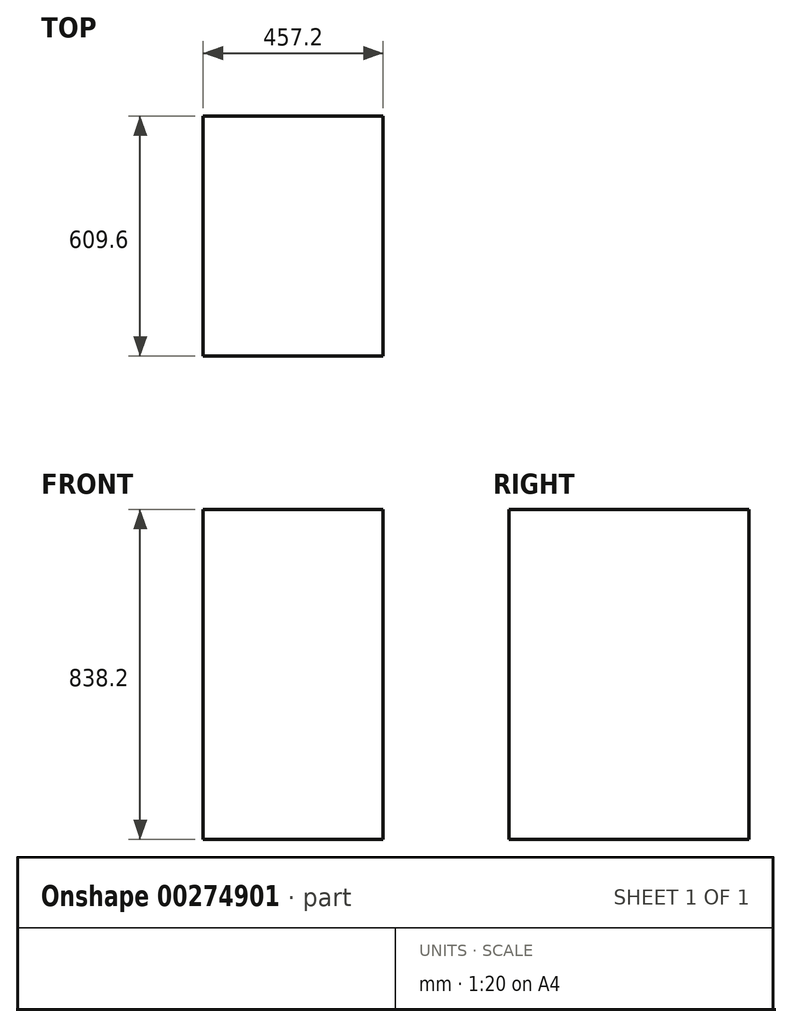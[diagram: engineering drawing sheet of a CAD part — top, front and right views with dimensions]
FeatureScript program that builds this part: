
annotation { "Feature Type Name" : "Feature", "Feature Type Description" : "" }
export const myFeature = defineFeature(function(context is Context, id is Id, definition is map)
    precondition{}
    {
        {
            var Q0;
            Q0=qCreatedBy(makeId("Top.planeOp"),FACE);
            var sketch = newSketch(context, id + "F0", { "sketchPlane" : qUnion([Q0])});
            skLineSegment(sketch, "E0.bottom", {"start": v(0, 0) * mm, "end": v(457.2, 0) * mm});
            skLineSegment(sketch, "E0.top", {"start": v(0, 609.6) * mm, "end": v(457.2, 609.6) * mm});
            skLineSegment(sketch, "E0.left", {"start": v(0, 0) * mm, "end": v(0, 609.6) * mm});
            skLineSegment(sketch, "E0.right", {"start": v(457.2, 0) * mm, "end": v(457.2, 609.6) * mm});
            skSolve(sketch);
        }
        {
            var Q0;
            Q0=makeQuery(id+"F0.imprint","IMPRINT",FACE,{"disambiguationData":[TD([[makeQuery(id+"F0.imprint","IMPRINT",EDGE,{"derivedFrom":sQuery(id+"F0.wireOp",EDGE,"E0.bottom")}),1.0]])]});
            extrude(context, id + "F1", {"entities" : qUnion([Q0]), "depth" : 838.2 * mm});
        }
    });
